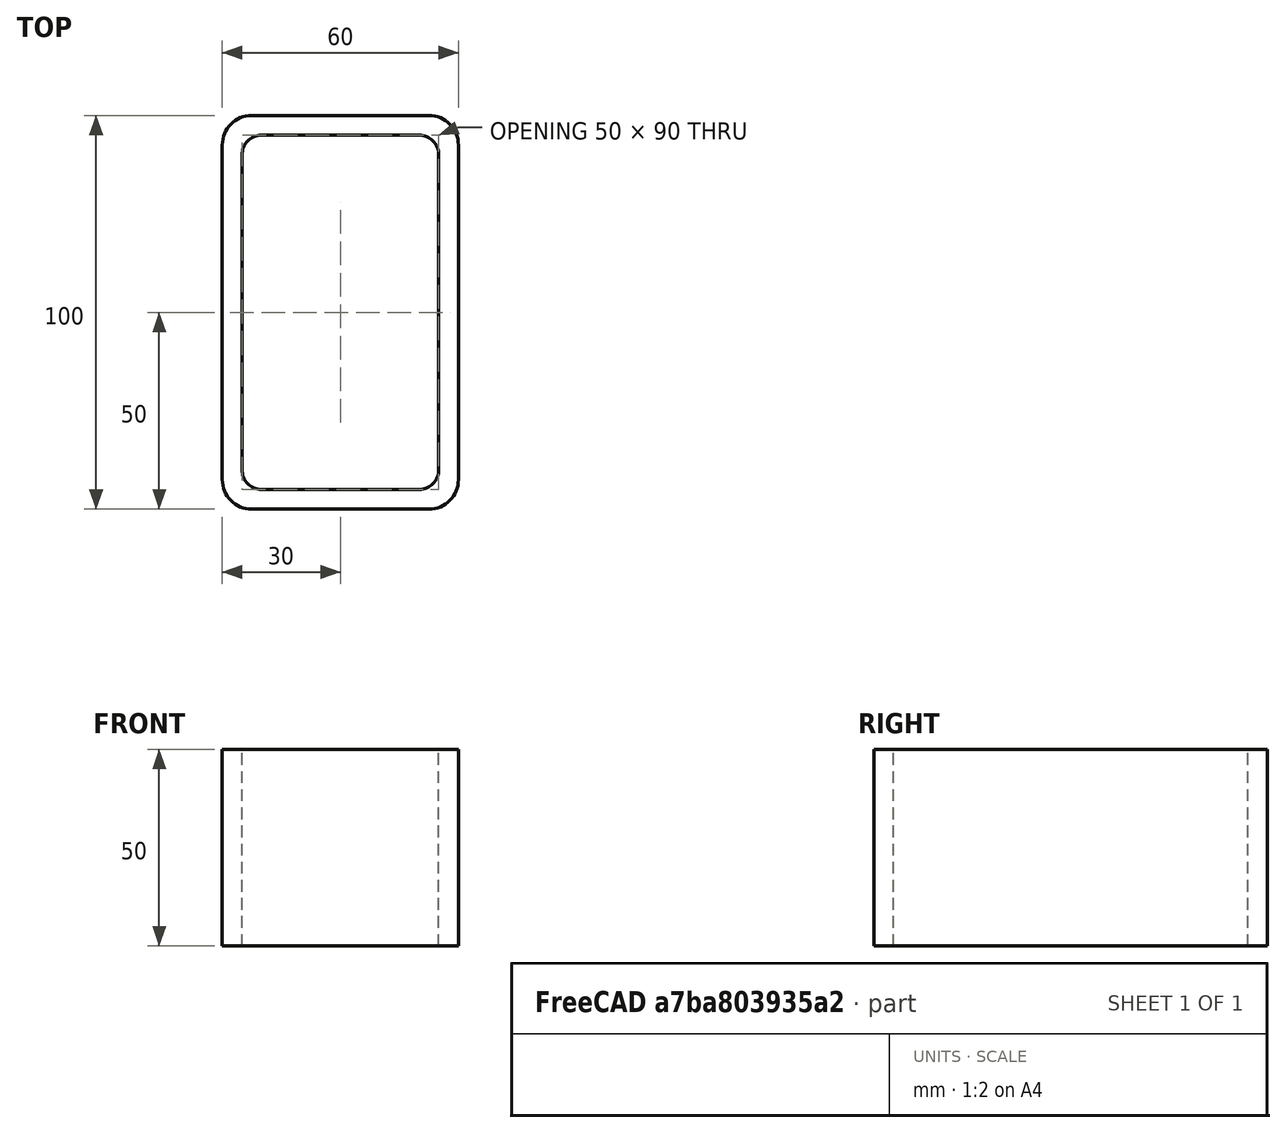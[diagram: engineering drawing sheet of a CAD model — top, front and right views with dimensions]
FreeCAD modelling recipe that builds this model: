
FCSTD DOCUMENT  (FreeCAD 0.15R4671 (Git))
Label: Rectangular hollow section 100x60x5 EN10219 S235JRH
License: All rights reserved
LicenseURL: http://en.wikipedia.org/wiki/All_rights_reserved
objects: Sketcher::SketchObject×1, Part::Extrusion×1
note: 2 computed .brp shape members not serialized (recipe doc carries the construction recipe); baked Part::Feature solids carry a one-line shape summary decoded from their .brp

FEATURE [Sketcher::SketchObject] Sketch
  sketch-geometry (16):
    g0: LineSegment StartX=-20 StartY=45 StartZ=0 EndX=20 EndY=45 EndZ=0
    g1: LineSegment StartX=25 StartY=40 StartZ=0 EndX=25 EndY=-40 EndZ=0
    g2: LineSegment StartX=20 StartY=-45 StartZ=0 EndX=-20 EndY=-45 EndZ=0
    g3: LineSegment StartX=-25 StartY=-40 StartZ=0 EndX=-25 EndY=40 EndZ=0
    g4: LineSegment StartX=-22.5 StartY=50 StartZ=0 EndX=22.5 EndY=50 EndZ=0
    g5: LineSegment StartX=30 StartY=42.5 StartZ=0 EndX=30 EndY=-42.5 EndZ=0
    g6: LineSegment StartX=22.5 StartY=-50 StartZ=0 EndX=-22.5 EndY=-50 EndZ=0
    g7: LineSegment StartX=-30 StartY=-42.5 StartZ=0 EndX=-30 EndY=42.5 EndZ=0
    g8: ArcOfCircle CenterX=-20 CenterY=40 CenterZ=0 NormalX=0 NormalY=0 NormalZ=1 Radius=5 StartAngle=1.5708 EndAngle=3.14159
    g9: ArcOfCircle CenterX=20 CenterY=40 CenterZ=0 NormalX=0 NormalY=0 NormalZ=1 Radius=5 StartAngle=0 EndAngle=1.5708
    g10: ArcOfCircle CenterX=20 CenterY=-40 CenterZ=0 NormalX=0 NormalY=0 NormalZ=1 Radius=5 StartAngle=4.71239 EndAngle=6.28319
    g11: ArcOfCircle CenterX=-20 CenterY=-40 CenterZ=0 NormalX=0 NormalY=0 NormalZ=1 Radius=5 StartAngle=3.14159 EndAngle=4.71239
    g12: ArcOfCircle CenterX=22.5 CenterY=42.5 CenterZ=0 NormalX=0 NormalY=0 NormalZ=1 Radius=7.5 StartAngle=0 EndAngle=1.5708
    g13: ArcOfCircle CenterX=22.5 CenterY=-42.5 CenterZ=0 NormalX=0 NormalY=0 NormalZ=1 Radius=7.5 StartAngle=4.71239 EndAngle=6.28319
    g14: ArcOfCircle CenterX=-22.5 CenterY=-42.5 CenterZ=0 NormalX=0 NormalY=0 NormalZ=1 Radius=7.5 StartAngle=3.14159 EndAngle=4.71239
    g15: ArcOfCircle CenterX=-22.5 CenterY=42.5 CenterZ=0 NormalX=0 NormalY=0 NormalZ=1 Radius=7.5 StartAngle=1.5708 EndAngle=3.14159
  constraints (36):
    c: Horizontal(g2)
    c: Vertical(g3)
    c: Horizontal(g6)
    c: Vertical(g7)
    c: Tangent(g3,g8) = 1.5708
    c: Tangent(g0,g8) = 1.5708
    c: Tangent(g0,g9) = 1.5708
    c: Tangent(g1,g9) = 1.5708
    c: Tangent(g1,g10) = 1.5708
    c: Tangent(g2,g10) = 1.5708
    c: Tangent(g2,g11) = 1.5708
    c: Tangent(g3,g11) = 1.5708
    c: Tangent(g4,g12) = 1.5708
    c: Tangent(g5,g12) = 1.5708
    c: Tangent(g5,g13) = 1.5708
    c: Tangent(g6,g13) = 1.5708
    c: Tangent(g6,g14) = 1.5708
    c: Tangent(g7,g14) = 1.5708
    c: Tangent(g7,g15) = 1.5708
    c: Tangent(g4,g15) = 1.5708
    c: Equal(g9,g8)
    c: Equal(g9,g11)
    c: Equal(g9,g10)
    c: Equal(g12,g15)
    c: Equal(g12,g14)
    c: Equal(g12,g13)
    c: Symmetric(g4,g6,g-1)
    c: Symmetric(g7,g5,g-2)
    c: DistanceY(g4,g6) = -100
    c: DistanceX(g7,g5) = 60
    c: Symmetric(g3,g1,g-2)
    c: Symmetric(g0,g2,g-1)
    c: DistanceY(g0,g4) = 5
    c: DistanceX(g5,g1) = -5
    c: Radius(g9) = 5
    c: Radius(g12) = 7.5
FEATURE [Part::Extrusion] Extrude  label="Rectangular hollow section 100x60x5 EN10219 S235JRH"
  Base = -> Sketch
  Dir = (0,0,50)
  Solid = true
